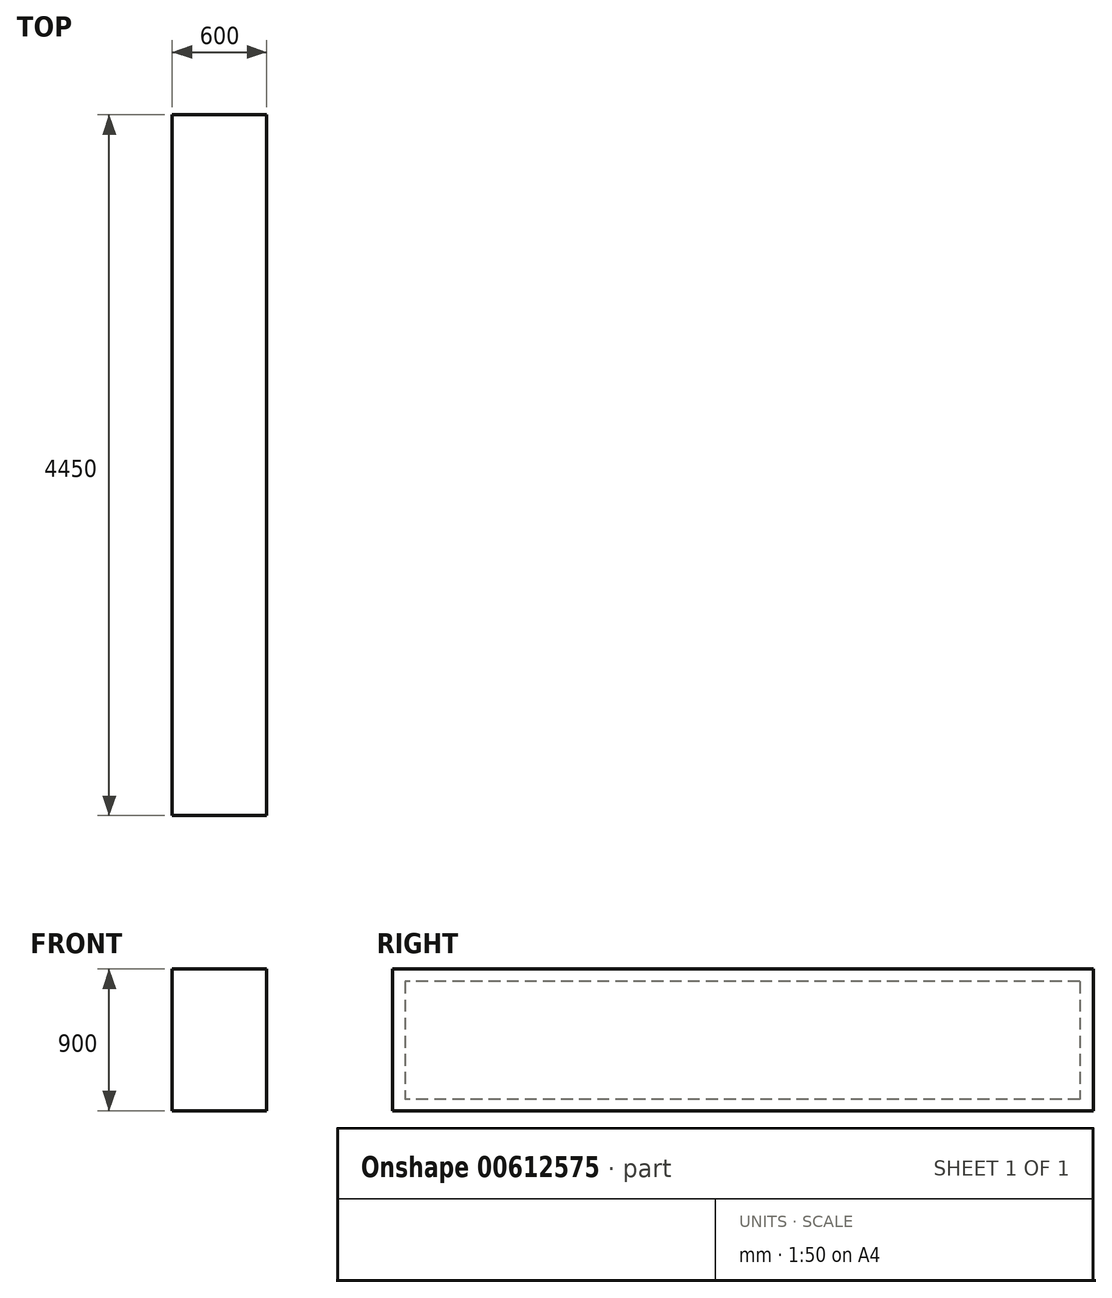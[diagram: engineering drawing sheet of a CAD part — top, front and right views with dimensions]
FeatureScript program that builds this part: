
annotation { "Feature Type Name" : "Feature", "Feature Type Description" : "" }
export const myFeature = defineFeature(function(context is Context, id is Id, definition is map)
    precondition{}
    {
        {
            var Q0;
            Q0=qCreatedBy(makeId("Front.planeOp"),FACE);
            var sketch = newSketch(context, id + "F0", { "sketchPlane" : qUnion([Q0])});
            skLineSegment(sketch, "E0.bottom", {"start": v(0, 0) * mm, "end": v(600, 0) * mm});
            skLineSegment(sketch, "E0.top", {"start": v(0, 900) * mm, "end": v(600, 900) * mm});
            skLineSegment(sketch, "E0.left", {"start": v(0, 0) * mm, "end": v(0, 900) * mm});
            skLineSegment(sketch, "E0.right", {"start": v(600, 0) * mm, "end": v(600, 900) * mm});
            skSolve(sketch);
        }
        {
            var Q0;
            Q0=makeQuery(id+"F0.imprint","IMPRINT",FACE,{"disambiguationData":[TD([[makeQuery(id+"F0.imprint","IMPRINT",EDGE,{"derivedFrom":sQuery(id+"F0.wireOp",EDGE,"E0.bottom")}),1.0]])]});
            extrude(context, id + "F1", {"entities" : qUnion([Q0]), "depth" : 5000 * mm - 550 * mm, "offsetDistance" : 25.4 * mm});
        }
        {
            var Q0;
            Q0=makeQuery(id+"F1.opExtrude","SWEPT_FACE",FACE,{"disambiguationData":[OSD([sQuery(id+"F0.wireOp",EDGE,"E0.left")])]});
            var sketch = newSketch(context, id + "F2", { "sketchPlane" : qUnion([Q0])});
            skLineSegment(sketch, "E1.bottom", {"start": v(85.19, 820.13) * mm, "end": v(4372.52, 820.13) * mm});
            skLineSegment(sketch, "E1.top", {"start": v(85.19, 72.16) * mm, "end": v(4372.52, 72.16) * mm});
            skLineSegment(sketch, "E1.left", {"start": v(85.19, 820.13) * mm, "end": v(85.19, 72.16) * mm});
            skLineSegment(sketch, "E1.right", {"start": v(4372.52, 820.13) * mm, "end": v(4372.52, 72.16) * mm});
            skSolve(sketch);
        }
        {
            var Q0;
            Q0=makeQuery(id+"F2.imprint","IMPRINT",FACE,{"disambiguationData":[TD([[makeQuery(id+"F2.imprint","IMPRINT",EDGE,{"derivedFrom":sQuery(id+"F2.wireOp",EDGE,"E1.bottom")}),-1.0]])]});
            extrude(context, id + "F3", {"entities" : qUnion([Q0]), "operationType" : NewBodyOperationType.REMOVE, "oppositeDirection" : true, "depth" : 2 * mm, "offsetDistance" : 25.4 * mm});
        }
    });
